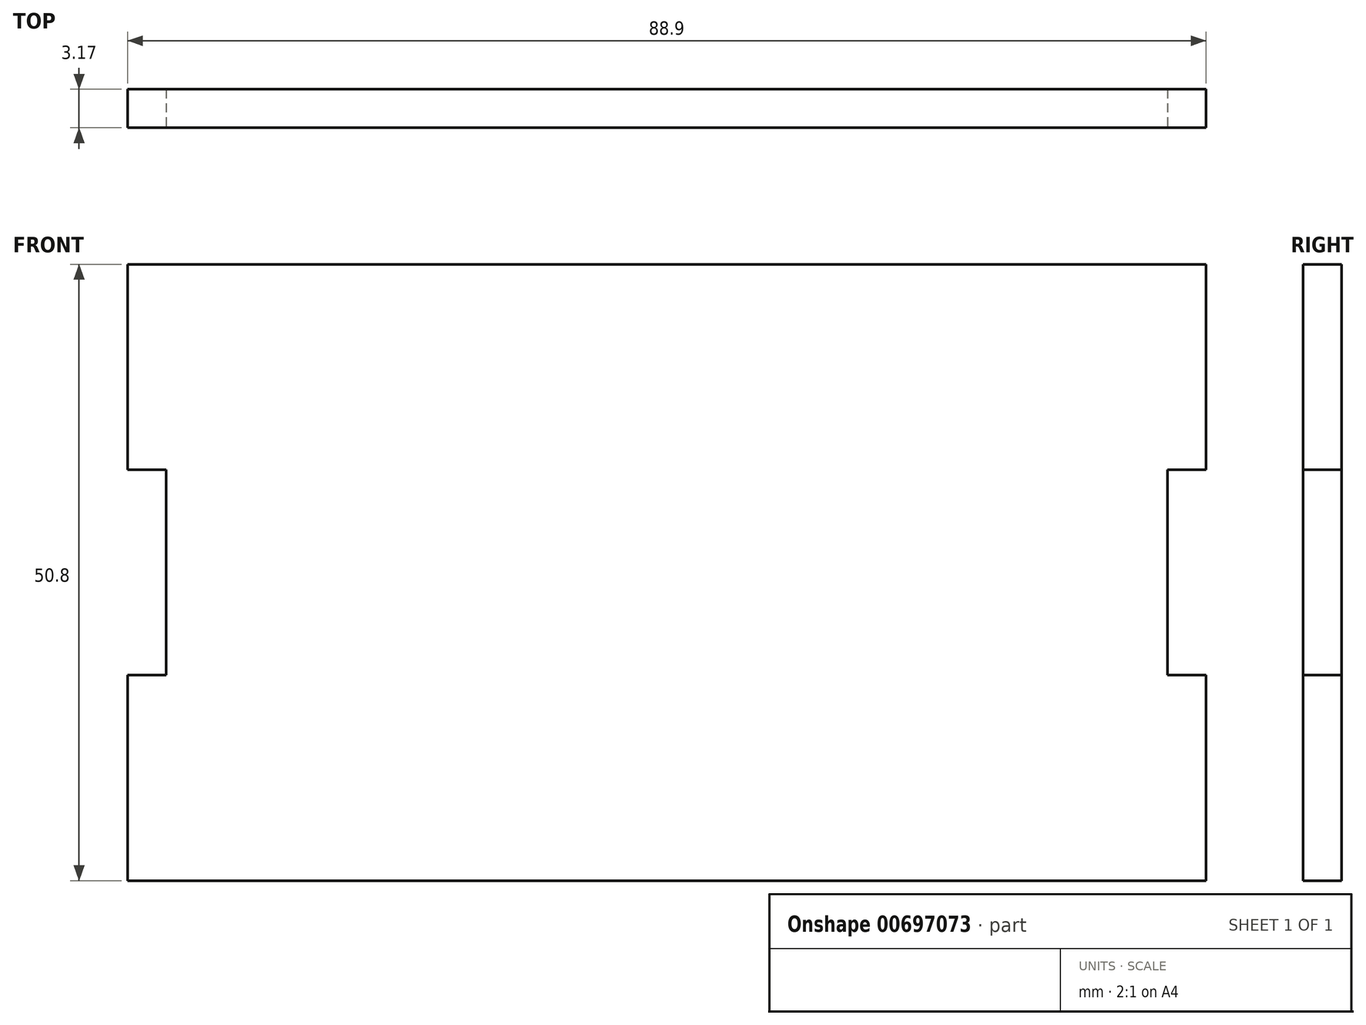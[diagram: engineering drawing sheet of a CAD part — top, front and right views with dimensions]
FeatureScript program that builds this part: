
annotation { "Feature Type Name" : "Feature", "Feature Type Description" : "" }
export const myFeature = defineFeature(function(context is Context, id is Id, definition is map)
    precondition{}
    {
        {
            var Q0;
            Q0=qCreatedBy(makeId("Front.planeOp"),FACE);
            var sketch = newSketch(context, id + "F0", { "sketchPlane" : qUnion([Q0])});
            skLineSegment(sketch, "E0.bottom", {"start": v(44.45, 25.4) * mm, "end": v(-44.45, 25.4) * mm});
            skLineSegment(sketch, "E0.top", {"start": v(44.45, -25.4) * mm, "end": v(-44.45, -25.4) * mm});
            skLineSegment(sketch, "E0.left", {"start": v(44.45, 25.4) * mm, "end": v(44.45, -25.4) * mm});
            skLineSegment(sketch, "E0.right", {"start": v(-44.45, 25.4) * mm, "end": v(-44.45, -25.4) * mm});
            skPoint(sketch, "E0.middle", {"position": v(0, 0) * mm});
            skSolve(sketch);
        }
        {
            var Q0;
            Q0 = qSketchRegion(id + "F0", true);
            extrude(context, id + "F1", {"entities" : qUnion([Q0]), "depth" : 3.17 * mm, "offsetDistance" : 25.4 * mm});
        }
        {
            var Q0;
            Q0=makeQuery(id+"F1.opExtrude","CAP_FACE",FACE,{"disambiguationData":[OSD([sQuery(id+"F0.wireOp",EDGE,"E0.bottom"),sQuery(id+"F0.wireOp",EDGE,"E0.top"),sQuery(id+"F0.wireOp",EDGE,"E0.left"),sQuery(id+"F0.wireOp",EDGE,"E0.right")])],"isStart":false});
            var sketch = newSketch(context, id + "F2", { "sketchPlane" : qUnion([Q0])});
            skLineSegment(sketch, "E1", {"start": v(41.28, 25.4) * mm, "end": v(41.28, 8.47) * mm, "construction": true});
            skLineSegment(sketch, "E2", {"start": v(41.28, 8.47) * mm, "end": v(41.28, -8.47) * mm, "construction": true});
            skLineSegment(sketch, "E3", {"start": v(41.28, -8.47) * mm, "end": v(41.28, -25.4) * mm, "construction": true});
            skLineSegment(sketch, "E4.bottom", {"start": v(41.28, 8.47) * mm, "end": v(44.45, 8.47) * mm});
            skLineSegment(sketch, "E4.top", {"start": v(41.28, -8.47) * mm, "end": v(44.45, -8.47) * mm});
            skLineSegment(sketch, "E4.left", {"start": v(41.28, 8.47) * mm, "end": v(41.28, -8.47) * mm});
            skLineSegment(sketch, "E4.right", {"start": v(44.45, 8.47) * mm, "end": v(44.45, -8.47) * mm});
            skLineSegment(sketch, "E5", {"start": v(0, 25.4) * mm, "end": v(0, -25.4) * mm, "construction": true});
            skLineSegment(sketch, "E6.MirrorCS", {"start": v(-41.28, 8.47) * mm, "end": v(-44.45, 8.47) * mm});
            skLineSegment(sketch, "E7.MirrorCS", {"start": v(-41.28, 8.47) * mm, "end": v(-41.28, -8.47) * mm, "construction": true});
            skLineSegment(sketch, "E8.MirrorCS", {"start": v(-44.45, 8.47) * mm, "end": v(-44.45, -8.47) * mm});
            skLineSegment(sketch, "E9.MirrorCS", {"start": v(-41.28, -8.47) * mm, "end": v(-44.45, -8.47) * mm});
            skLineSegment(sketch, "E10", {"start": v(-41.28, 8.47) * mm, "end": v(-41.28, -8.47) * mm});
            skSolve(sketch);
        }
        {
            var Q0;
            Q0=makeQuery(id+"F2.imprint","IMPRINT",FACE,{"disambiguationData":[TD([[makeQuery(id+"F2.imprint","IMPRINT",EDGE,{"derivedFrom":sQuery(id+"F2.wireOp",EDGE,"E4.bottom")}),-1.0]])]});
            var Q1;
            Q1=makeQuery(id+"F2.imprint","IMPRINT",FACE,{"disambiguationData":[TD([[makeQuery(id+"F2.imprint","IMPRINT",EDGE,{"derivedFrom":sQuery(id+"F2.wireOp",EDGE,"E6.MirrorCS")}),1.0]])]});
            extrude(context, id + "F3", {"entities" : qUnion([Q0, Q1]), "operationType" : NewBodyOperationType.REMOVE, "oppositeDirection" : true, "depth" : 3.17 * mm, "offsetDistance" : 25.4 * mm});
        }
    });
